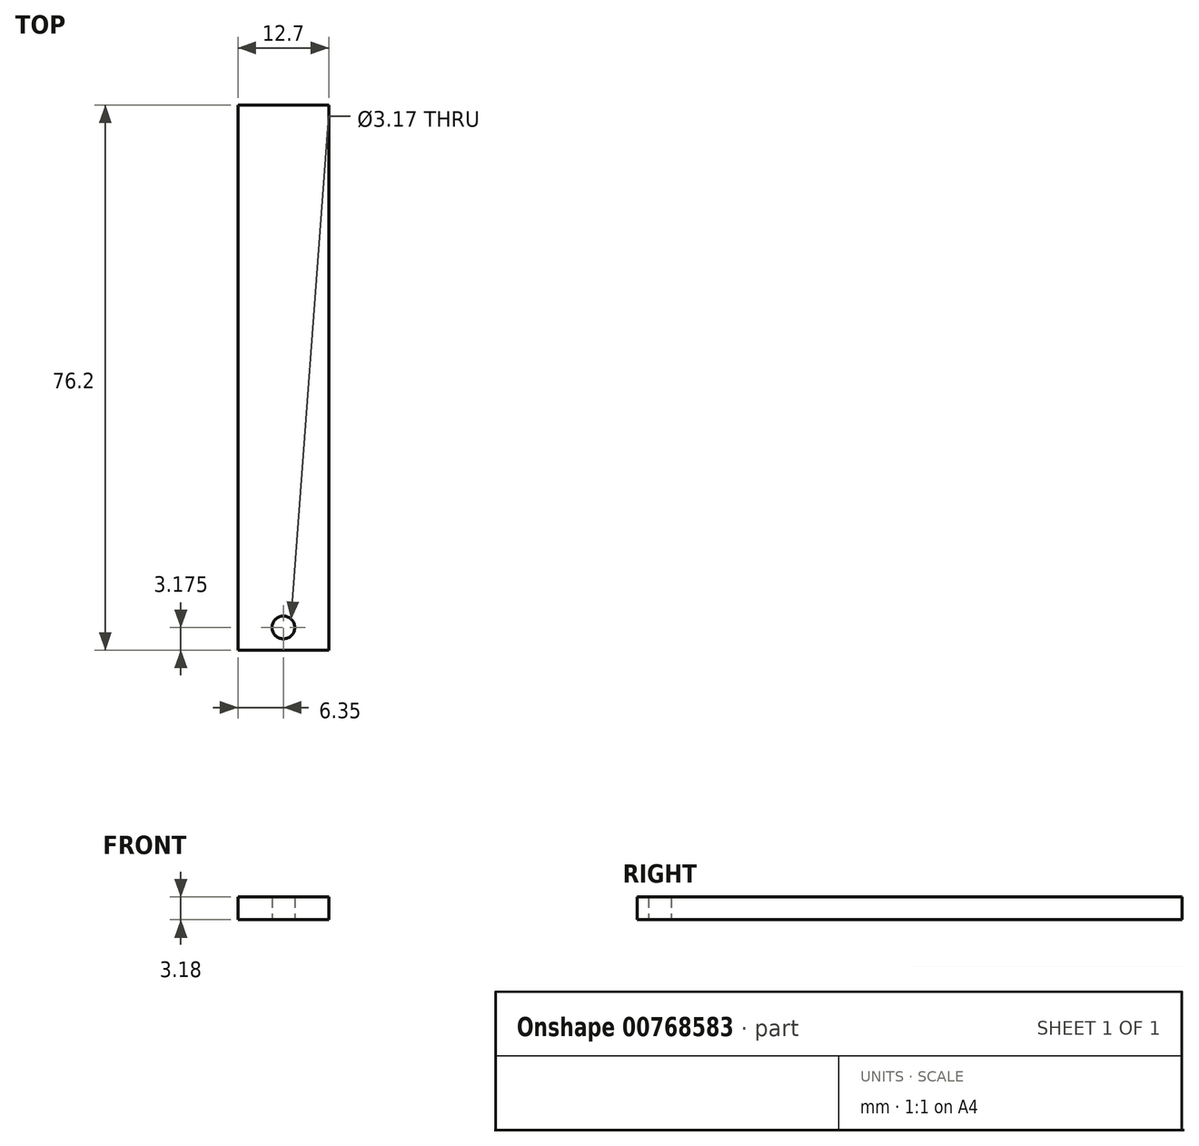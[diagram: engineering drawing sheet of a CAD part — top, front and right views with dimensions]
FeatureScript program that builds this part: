
annotation { "Feature Type Name" : "Feature", "Feature Type Description" : "" }
export const myFeature = defineFeature(function(context is Context, id is Id, definition is map)
    precondition{}
    {
        {
            var Q0;
            Q0=qCreatedBy(makeId("Top.planeOp"),FACE);
            var sketch = newSketch(context, id + "F0", { "sketchPlane" : qUnion([Q0])});
            skLineSegment(sketch, "E0.bottom", {"start": v(6.35, -38.1) * mm, "end": v(-6.35, -38.1) * mm});
            skLineSegment(sketch, "E0.top", {"start": v(6.35, 38.1) * mm, "end": v(-6.35, 38.1) * mm});
            skLineSegment(sketch, "E0.left", {"start": v(6.35, -38.1) * mm, "end": v(6.35, 38.1) * mm});
            skLineSegment(sketch, "E0.right", {"start": v(-6.35, -38.1) * mm, "end": v(-6.35, 38.1) * mm});
            skPoint(sketch, "E0.middle", {"position": v(0, 0) * mm});
            skCircle(sketch, "E1", {"center": v(0, -34.93) * mm, "radius": 1.59 * mm});
            skSolve(sketch);
        }
        {
            var Q0;
            Q0=makeQuery(id+"F0.imprint","IMPRINT",FACE,{"disambiguationData":[TD([[makeQuery(id+"F0.imprint","IMPRINT",EDGE,{"derivedFrom":sQuery(id+"F0.wireOp",EDGE,"E0.bottom")}),-1.0]])]});
            extrude(context, id + "F1", {"entities" : qUnion([Q0]), "depth" : 3.17 * mm, "offsetDistance" : 25.4 * mm});
        }
    });
